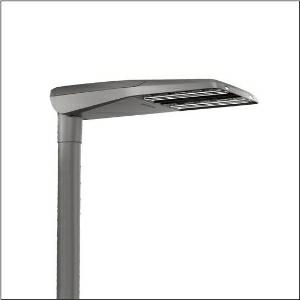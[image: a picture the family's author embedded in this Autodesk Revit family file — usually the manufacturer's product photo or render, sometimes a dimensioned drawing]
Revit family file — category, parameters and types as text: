
# Revit family: streetlight_sl_11_iq_midi___st1_2a_5xc3a61f08me_e1b3
name_source: partatom
category: Lighting Fixtures
units: mm (PartAtom-declared; Revit-internal decimal feet)

## family parameters
Cut with Voids When Loaded = No
Host = Face
Light Source = No
Part Type = Normal
Room Calculation Point = No
Round Connector Dimension = Use Diameter
Shared = No

## types (1)
- --- (1 x LED, 16120 lm, 123.9 W, 2700K)
    Apparent Load = 124 VA
    CIE Flux Codes = 32 70 96 100 100
    Color Rendering = 70
    Color Temperature = 2700K
    Default Elevation = 1800 mm
    Description = Streetlight SL 11 iQ midi, mast luminaire, primary light control with 3 zone facetted reflector, of plastic, silver coated, highly specular, primary optical cover: cover, of PMMA, transparent, light distribution: ST1.2a, light emission: direct distribution, primary light characteristic: asymmetric, installation type: post-top, side-entry, lamps: LED, High Power LED, rated values: 16.120lm | 123,9W | 130,1lm/W (begin service life); end service life: 16.120lm | 130,9W; at 50% lumin. flux: 8.060lm | 56,7W | 142,2lm/W, colour temperature: 2700K, colour rendering: CRI > 70, light colour: 727, light setting 1 begin service life: 100% | 16.120lm | 123,9W | 130,1lm/W | 2.700K, light setting 1 end service life: 130,9W, further light settings possible, control: Street-Remote, Auto-Match, Temp-Guard, Lumen-Switch, Night-Set, Smart-Wire, Light-Fading, Desk-Remote (wireless, voltage-free reading and setting of iQ features in the workshop via application-optimized NFC function/RFID function), optimised constant luminous flux control (CLO 2.0), with cable H07RN-F 5x 1.5mm², mains connection: 230..240V, AC, 50/60Hz, connection cable pre-assembled, cable length: 12,5m, luminaire housing, of diecast aluminium, powder-coated, Siteco® metallic grey (DB 702S), please order mast flange separately, inclination adjustable without tools: 0°, 5°, 10°, 15° (post-top) | 0°, -5°, -10°, -15° (side-entry), sealing non-destructively replaceable, multi-level sealing system, length: 780mm, width: 376mm, height: 118mm, mast flange for spigot size: 42mm (side-entry): 5XC10008XM4, 60/48mm (side-entry/post-top): 5XC10108XM2, 76/60mm (side-entry/post-top): 5XC10108XM1, equipment: Power, protection rating (complete): IP66, insulation class (complete): insulation class II (safety insulation), certification: CE, ENEC, ENEC+, VDE, impact resistance: IK10, permissible operating ambient temperature for outdoor applications: -25..+50°C, standard-compliant lighting for roads and squares, Environmental Product Declaration (EPD) tested and certified by an independent institute, packaging unit: 1 piece

Light Distribution: ST1.2a
    Height = 118 mm
    Lamp = 1 x LED
    Lamp Light Flux = 16120 lm
    Lamp Power = 123.9 W
    Lamp count = 1
    Length = 780 mm
    Luminous efficacy = 130 lm/W
    Manufacturer = Siteco
    ModVariant = No
    Model = 5XC3A61F08ME
    Number of Poles = 1
    OnlyDefault = Yes
    Power Factor = 1
    Product Name = Streetlight SL 11 iQ midi | ST1.2a
    Product group = mast luminaire | pylon top
    ProductGroupID = 6100
    Protection Class = Protection class II
    Protection Degree = IP 66
    RLX_Detail_Level = 1
    RLX_Emergency_Light_Flux = 0 lm
    RLX_Emergency_Type = 0
    RLX_Emergency_Type_DB = No
    RlxData = <blob elided: 71081 chars, md5=6baf8b6d>
    Socket = socket
    Standby Power = 0 W
    System Light Flux = 16119 lm
    System Power = 124 W
    Type Comments = factory setting: luminous flux: 100 % | dim-lin: 254 | 554 mA
    Type Image = l_1005960.jpg
    URL = http://relux.com
    VarID = @adj_099819
    Voltage = 0 V
    Weight = 0.00 kg
    Width = 376 mm

## geometry (parser evidence)
native form markers: Blend x4, Sweep x10
no freeform markers — native parametric forms only
